# Revit family: MNTHT
name_source: partatom
category: Lighting Fixtures
units: mm (PartAtom-declared; Revit-internal decimal feet)

## family parameters
Always vertical = Yes
Cut with Voids When Loaded = No
Host = Wall
Light Source = Yes
Maintain Annotation Orientation = No
Part Type = Normal
Room Calculation Point = No
Round Connector Dimension = Use Diameter
Shared = No

## types (4) — shared parameters
Color Filter = 16777215
Default Elevation = 0' - 0"
Description = WALL MOUNTED LUMINAIRE
Dimming Lamp Color Temperature Shift = <None>
Emit from Line Length = 2' - 0"
Keynote = MNT
LED BOARD MATERIAL = LED BOARD MATERIAL
LED MATERIAL = LED MATERIAL
LENS MATERIAL = LENS MATERIAL
MOUNTING HEIGHT = 7' - 5"
Model = MNTHT
Photometric Web File = MNTHT.IES
Tilt Angle = 90.00°
Type Image = MNT IMAGE.png

## per-type parameters (varying)
| type | HOUSING MATERIAL |
| MNTHT-SILVER-HT-SA-SE | HOUSING MATERIAL GRAY |
| MNTHT-WHITE-HT-SA-SE | HOUSING MATERIAL WHITE |
| MNTHT-BLACK-HT-SA-SE | HOUSING MATERIAL BLACK |
| MNTHT-BROWN-HT-SA-SE | HOUSING MATERIAL BROWN |

## geometry (parser evidence)
native form markers: Sweep x10
no freeform markers — native parametric forms only
